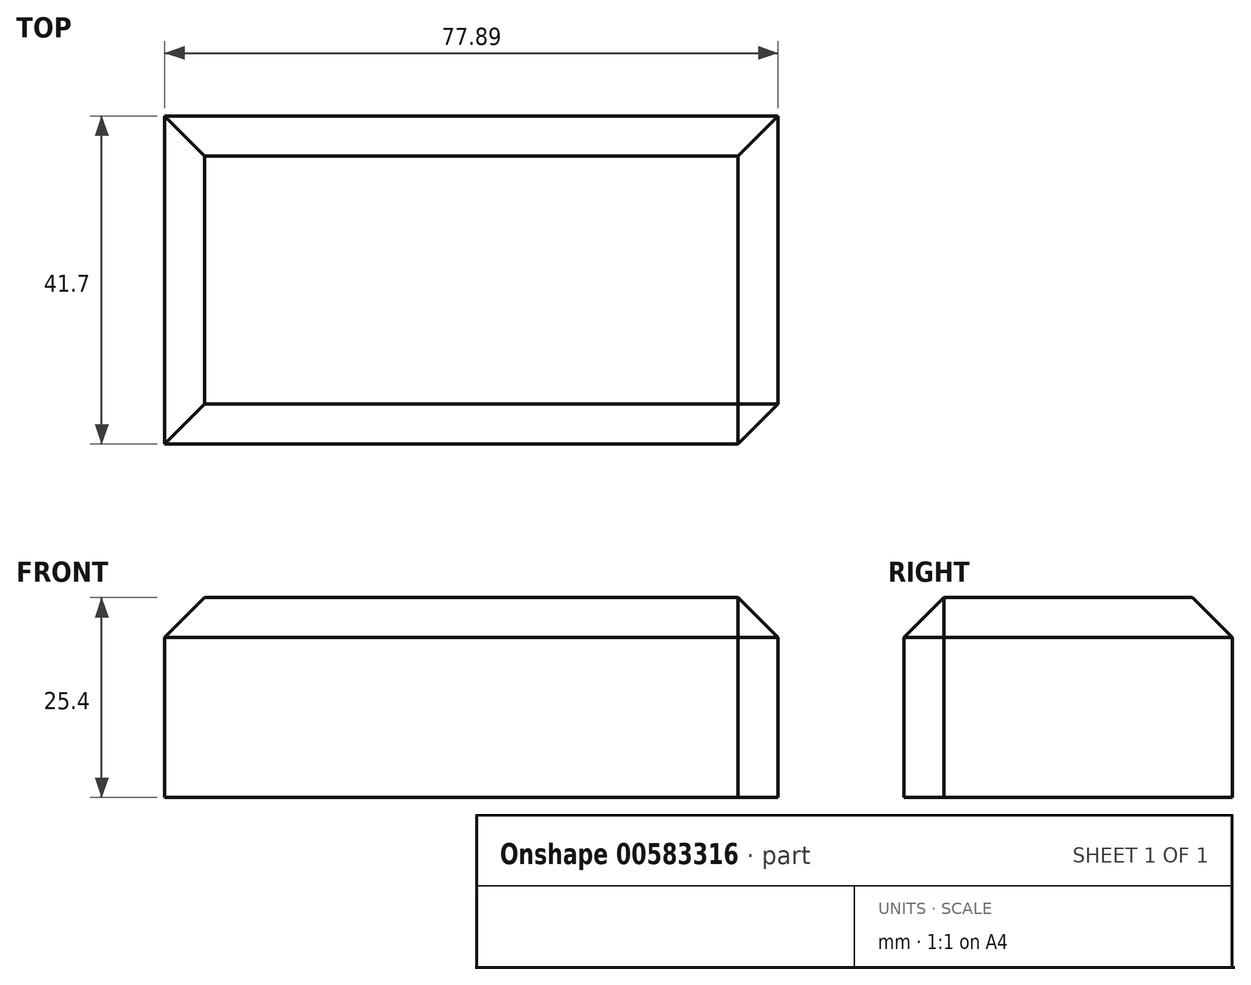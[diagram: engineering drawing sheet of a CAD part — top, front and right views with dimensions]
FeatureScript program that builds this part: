
annotation { "Feature Type Name" : "Feature", "Feature Type Description" : "" }
export const myFeature = defineFeature(function(context is Context, id is Id, definition is map)
    precondition{}
    {
        {
            var Q0;
            Q0=qCreatedBy(makeId("Top.planeOp"),FACE);
            var sketch = newSketch(context, id + "F0", { "sketchPlane" : qUnion([Q0])});
            skLineSegment(sketch, "E0.bottom", {"start": v(-117.1, -7.63) * mm, "end": v(-39.2, -7.63) * mm});
            skLineSegment(sketch, "E0.top", {"start": v(-117.1, -49.33) * mm, "end": v(-39.2, -49.33) * mm});
            skLineSegment(sketch, "E0.left", {"start": v(-117.1, -7.63) * mm, "end": v(-117.1, -49.33) * mm});
            skLineSegment(sketch, "E0.right", {"start": v(-39.2, -7.63) * mm, "end": v(-39.2, -49.33) * mm});
            skSolve(sketch);
        }
        {
            var Q0;
            Q0=makeQuery(id+"F0.imprint","IMPRINT",FACE,{"disambiguationData":[TD([[makeQuery(id+"F0.imprint","IMPRINT",EDGE,{"derivedFrom":sQuery(id+"F0.wireOp",EDGE,"E0.bottom")}),-1.0]])]});
            extrude(context, id + "F1", {"entities" : qUnion([Q0]), "depth" : 25.4 * mm, "offsetDistance" : 25.4 * mm});
        }
        {
            var Q0;
            Q0=makeQuery(id+"F1.opExtrude","SWEPT_EDGE",EDGE,{"disambiguationData":[OSD([sQuery(id+"F0.wireOp",EDGE,"E0.top"),sQuery(id+"F0.wireOp",EDGE,"E0.right")])]});
            var Q1;
            Q1=makeQuery(id+"F1.opExtrude","CAP_EDGE",EDGE,{"disambiguationData":[OSD([sQuery(id+"F0.wireOp",EDGE,"E0.top")])],"isStart":false});
            var Q2;
            Q2=makeQuery(id+"F1.opExtrude","CAP_EDGE",EDGE,{"disambiguationData":[OSD([sQuery(id+"F0.wireOp",EDGE,"E0.right")])],"isStart":false});
            var Q3;
            Q3=makeQuery(id+"F1.opExtrude","CAP_EDGE",EDGE,{"disambiguationData":[OSD([sQuery(id+"F0.wireOp",EDGE,"E0.bottom")])],"isStart":false});
            var Q4;
            Q4=makeQuery(id+"F1.opExtrude","CAP_EDGE",EDGE,{"disambiguationData":[OSD([sQuery(id+"F0.wireOp",EDGE,"E0.left")])],"isStart":false});
            chamfer(context, id + "F2", {"entities" : qUnion([Q0, Q1, Q2, Q3, Q4]), "width" : 5.08 * mm, "tangentPropagation" : true});
        }
    });
